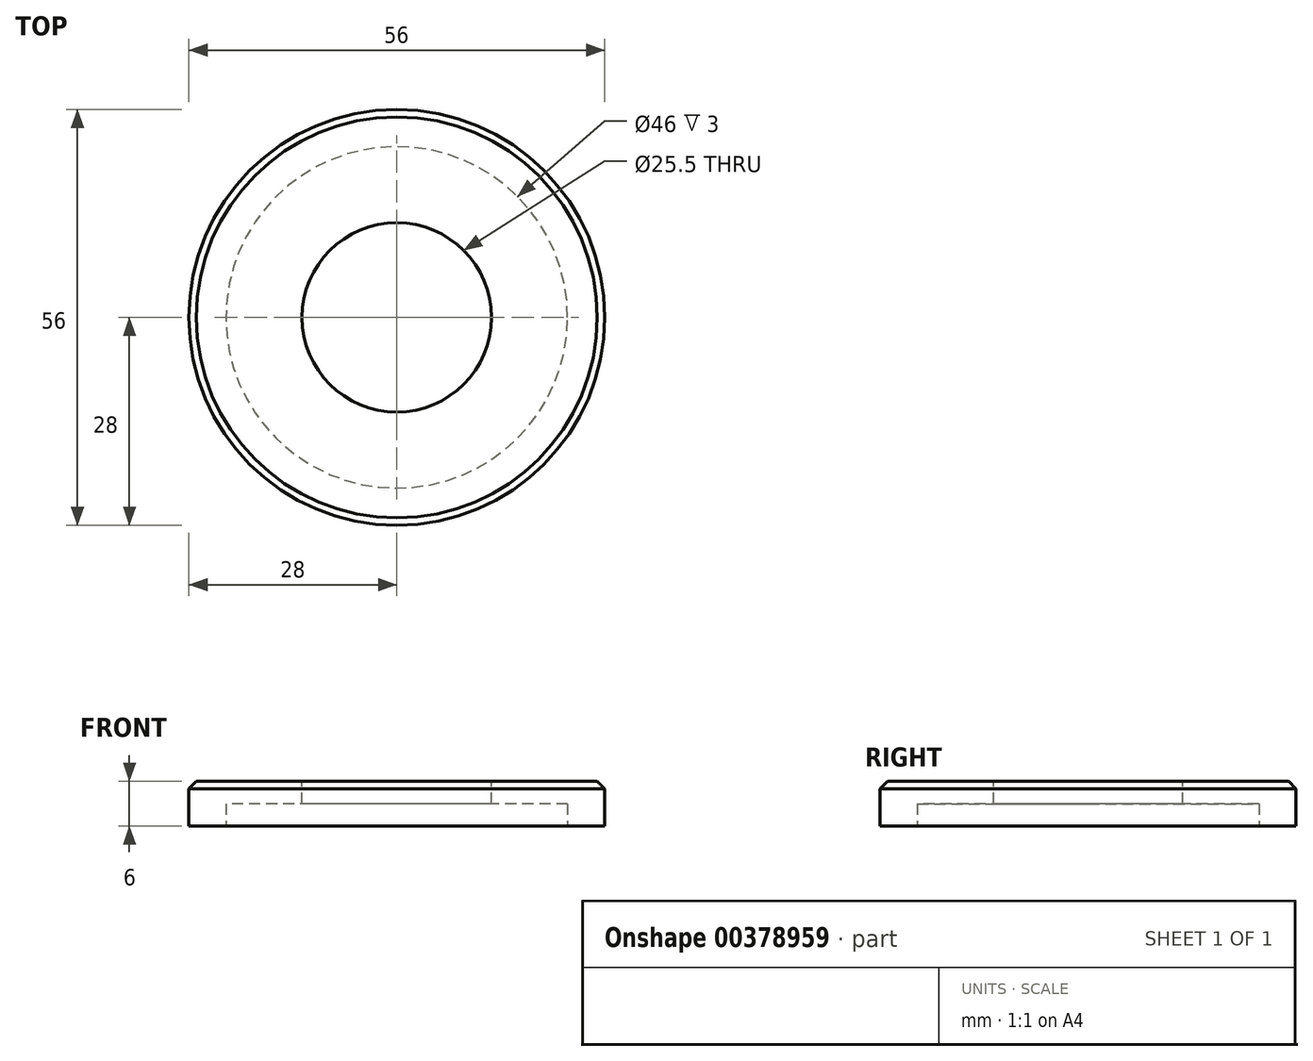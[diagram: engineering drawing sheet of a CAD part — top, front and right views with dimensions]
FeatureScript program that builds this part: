
annotation { "Feature Type Name" : "Feature", "Feature Type Description" : "" }
export const myFeature = defineFeature(function(context is Context, id is Id, definition is map)
    precondition{}
    {
        {
            var Q0;
            Q0=qCreatedBy(makeId("Top.planeOp"),FACE);
            var sketch = newSketch(context, id + "F0", { "sketchPlane" : qUnion([Q0])});
            skCircle(sketch, "E0", {"center": v(0, 0) * mm, "radius": 22.5 * mm, "construction": true});
            skCircle(sketch, "E1", {"center": v(0, 0) * mm, "radius": 23 * mm});
            skCircle(sketch, "E2.0", {"center": v(0, 0) * mm, "radius": 28 * mm});
            skSolve(sketch);
        }
        {
            var Q0;
            Q0=makeQuery(id+"F0.imprint","IMPRINT",FACE,{"disambiguationData":[TD([[makeQuery(id+"F0.imprint","IMPRINT",EDGE,{"derivedFrom":sQuery(id+"F0.wireOp",EDGE,"E1")}),1.0]])]});
            var Q1;
            Q1=makeQuery(id+"F0.imprint","IMPRINT",FACE,{"disambiguationData":[TD([[makeQuery(id+"F0.imprint","IMPRINT",EDGE,{"derivedFrom":sQuery(id+"F0.wireOp",EDGE,"E1")}),-1.0]])]});
            extrude(context, id + "F1", {"entities" : qUnion([Q0, Q1]), "depth" : 6 * mm});
        }
        {
            var Q0;
            Q0=makeQuery(id+"F0.imprint","IMPRINT",FACE,{"disambiguationData":[TD([[makeQuery(id+"F0.imprint","IMPRINT",EDGE,{"derivedFrom":sQuery(id+"F0.wireOp",EDGE,"E1")}),1.0]])]});
            extrude(context, id + "F2", {"entities" : qUnion([Q0]), "operationType" : NewBodyOperationType.REMOVE, "depth" : 3 * mm});
        }
        {
            var Q0;
            Q0=makeQuery(id+"F1.opExtrude","CAP_FACE",FACE,{"disambiguationData":[OSD([sQuery(id+"F0.wireOp",EDGE,"E2.0")])],"isStart":false});
            var sketch = newSketch(context, id + "F3", { "sketchPlane" : qUnion([Q0])});
            skCircle(sketch, "E3", {"center": v(0, 0) * mm, "radius": 12.75 * mm});
            skSolve(sketch);
        }
        {
            var Q0;
            Q0=qSketchRegion(id+"F3",true);
            extrude(context, id + "F4", {"entities" : qUnion([Q0]), "operationType" : NewBodyOperationType.REMOVE, "endBound" : BoundingType.THROUGH_ALL, "oppositeDirection" : true, "depth" : 25 * mm});
        }
        {
            var Q0;
            Q0=makeQuery(id+"F4.boolean.opBoolean","COPY",EDGE,{"derivedFrom":makeQuery(id+"F4.opExtrude","CAP_EDGE",EDGE,{"disambiguationData":[OSD([sQuery(id+"F3.wireOp",EDGE,"E3")])],"isStart":true})});
            var Q1;
            Q1=makeQuery(id+"F1.opExtrude","CAP_EDGE",EDGE,{"disambiguationData":[OSD([sQuery(id+"F0.wireOp",EDGE,"E2.0")])],"isStart":false});
            chamfer(context, id + "F5", {"entities" : qUnion([Q0, Q1]), "width" : 1 * mm, "tangentPropagation" : true});
        }
    });
